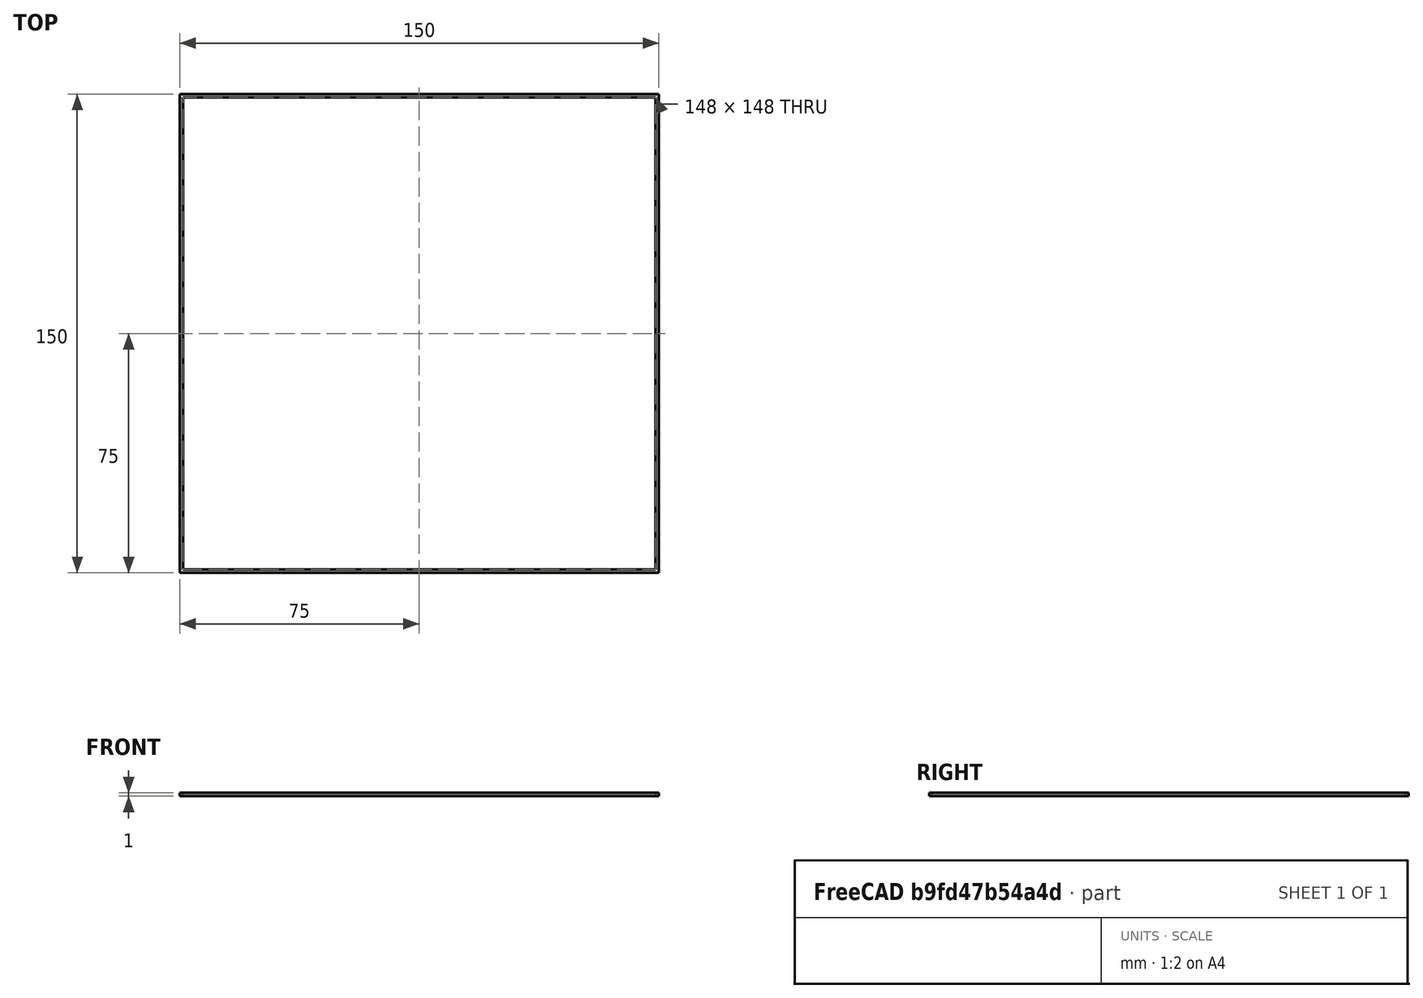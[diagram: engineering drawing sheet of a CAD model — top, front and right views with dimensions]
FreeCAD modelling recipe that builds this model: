
FCSTD DOCUMENT  (FreeCAD 0.18R14555 (Git shallow))
Label: level-test
License: All rights reserved
LicenseURL: http://en.wikipedia.org/wiki/All_rights_reserved
objects: Sketcher::SketchObject×1, PartDesign::Pad×1, PartDesign::Body×1
note: 4 computed .brp shape members not serialized (recipe doc carries the construction recipe); baked Part::Feature solids carry a one-line shape summary decoded from their .brp

FEATURE [Sketcher::SketchObject] Sketch
  MapMode = 5
  Support = -> [XY_Plane]
  sketch-geometry (11):
    g0: LineSegment StartX=0 StartY=0 StartZ=0 EndX=150 EndY=0 EndZ=0
    g1: LineSegment StartX=150 StartY=0 StartZ=0 EndX=150 EndY=150 EndZ=0
    g2: LineSegment StartX=150 StartY=150 StartZ=0 EndX=0 EndY=150 EndZ=0
    g3: LineSegment StartX=0 StartY=150 StartZ=0 EndX=0 EndY=0 EndZ=0
    g4: LineSegment StartX=1 StartY=1 StartZ=0 EndX=149 EndY=1 EndZ=0
    g5: LineSegment StartX=149 StartY=1 StartZ=0 EndX=149 EndY=149 EndZ=0
    g6: LineSegment StartX=149 StartY=149 StartZ=0 EndX=1 EndY=149 EndZ=0
    g7: LineSegment StartX=1 StartY=149 StartZ=0 EndX=1 EndY=1 EndZ=0
    g8: LineSegment [constr] StartX=1 StartY=149 StartZ=0 EndX=0 EndY=150 EndZ=0
    g9: LineSegment [constr] StartX=149 StartY=149 StartZ=0 EndX=150 EndY=150 EndZ=0
    g10: LineSegment [constr] StartX=0 StartY=0 StartZ=0 EndX=1 EndY=1 EndZ=0
  constraints (29):
    c: Coincident(g0,g1)
    c: Coincident(g1,g2)
    c: Coincident(g2,g3)
    c: Coincident(g3,g0)
    c: Horizontal(g0)
    c: Horizontal(g2)
    c: Vertical(g1)
    c: Vertical(g3)
    c: Coincident(g0,g-1)
    c: Coincident(g4,g5)
    c: Coincident(g5,g6)
    c: Coincident(g6,g7)
    c: Coincident(g7,g4)
    c: Horizontal(g4)
    c: Horizontal(g6)
    c: Vertical(g5)
    c: Vertical(g7)
    c: Equal(g2,g3)
    c: Equal(g7,g6)
    c: Coincident(g8,g6)
    c: Coincident(g8,g2)
    c: Coincident(g9,g5)
    c: Coincident(g9,g1)
    c: Coincident(g10,g0)
    c: Coincident(g10,g4)
    c: Equal(g10,g8)
    c: Equal(g8,g9)
    c: DistanceX(g2,g2) = 150
    c: DistanceX(g2,g6) = 1
FEATURE [PartDesign::Pad] Pad
  Length = 1
  Length2 = 100
  Profile = -> Sketch
  Type = 0
FEATURE [PartDesign::Body] Body
  Group = -> [Sketch,Pad]
  Origin = -> Origin
  Tip = -> Pad
